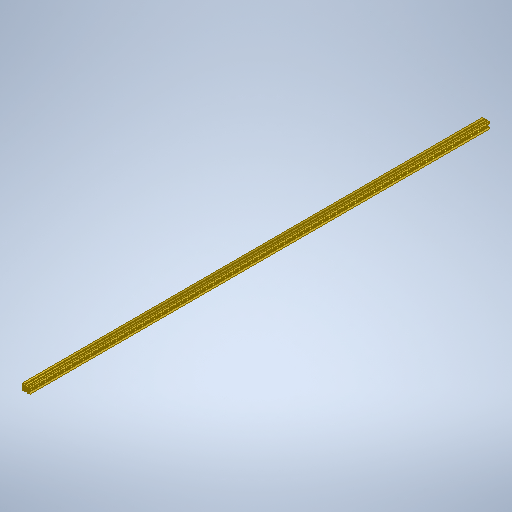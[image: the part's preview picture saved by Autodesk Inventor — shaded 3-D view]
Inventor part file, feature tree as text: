
AUTODESK INVENTOR PART (.ipt)
format: ipt  version: 2025.2 (Build 292293000, 293)  size: 430,080 bytes
history: native  units: mm
features: sketch x2, extrude x1, mirror x1
ambient origin geometry x8: Origin, YZ Plane, XZ Plane, XY Plane, X Axis, Y Axis, Z Axis, Center Point
bodies: Body1 (feature_tree)
feature tree (4):
  extrude  "Extrusão2"  Depth=30.0mm
  mirror  "Espelhar2"
  sketch  "Esboço1"  dims[d0=30.0mm d5=30.0mm]
  sketch  "Esboço - Padrão circular1"  dims[d6=15.0mm d7=10.0mm d8=8.2mm d9=8.0mm d11=2.0mm d13=0.5mm d19=5.0mm d23=1.1mm d26=11.5mm d27=2.2mm d28=1.1mm d29=1.1mm d33=2.2mm d34=2.2mm d35=40.0mm d37=360.0deg d39=1.1mm d44=2000.0mm d45=0.0mm d46=0.0mm d47=0.0mm d48=0.0mm d49=0.0mm]
